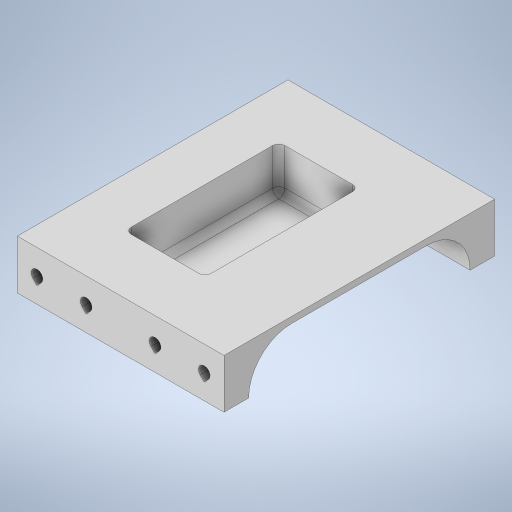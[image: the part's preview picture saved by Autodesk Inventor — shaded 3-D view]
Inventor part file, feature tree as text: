
AUTODESK INVENTOR PART (.ipt)
format: ipt  version: 2024 (Build 280153000, 153)  size: 775,168 bytes
history: native  units: in
note: dims shown in document units (in); Inventor stores cm internally (conversion verified against a paired STEP export)
features: extrude x7, sketch x7, projected_geometry x6, mirror x4, fillet x3, plane x2
ambient origin geometry x8: Origin, YZ Plane, XZ Plane, XY Plane, X Axis, Y Axis, Z Axis, Center Point
bodies: Solid1 (feature_tree)
feature tree (29):
  extrude  "Extrusion1"  Depth=4.2in
  extrude  "Extrusion2"  Depth=1.625in
  plane  "Work Plane1"
  plane  "Work Plane2"
  extrude  "Extrusion3"  Depth=1.0in
  mirror  "Mirror2"
  fillet  "Fillet1"  Radius=0.875in
  extrude  "Extrusion4"  Depth=0.3in
  mirror  "Mirror3"
  mirror  "Mirror4"
  extrude  "Extrusion5"  Depth=0.125in TaperAngle=0.0deg
  fillet  "Fillet2"  Radius=0.125in
  extrude  "Extrusion6"  Depth=0.2362in
  fillet  "Fillet3"  Radius=0.4in
  extrude  "Extrusion7"  Depth=0.125in
  mirror  "Mirror5"
  sketch  "Sketch1"  dims[d0=5.5in d1=4.2in]
  sketch  "Sketch2"  dims[d2=1.0in d3=0.0in d4=1.625in]
  projected_geometry  "Projected Loop1"
  sketch  "Sketch3"  dims[d5=3.125in d6=1.0in d7=0.875in d8=0.0in]
  projected_geometry  "Projected Loop2"
  sketch  "Sketch4"  dims[d9=0.1in d10=0.3in]
  projected_geometry  "Projected Loop3"
  sketch  "Sketch6"  dims[d11=0.1in d13=0.125in d14=0.0in d15=0.125in]
  projected_geometry  "Projected Loop4"
  sketch  "Sketch7"  dims[d16=0.1in d17=0.2362in d18=0.4in]
  projected_geometry  "Projected Loop5"
  sketch  "Sketch8"  dims[d20=0.4331in d21=0.0in d22=1.0in d23=0.125in d24=0.5in d25=0.5in d26=1.45in d27=0.0in d28=0.25in d29=0.125in d30=0.5in d31=0.5in d32=0.875in d33=0.0in d34=0.25in d35=1.0in d36=0.0in]
  projected_geometry  "Projected Loop6"
